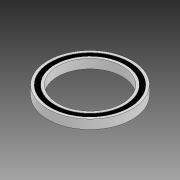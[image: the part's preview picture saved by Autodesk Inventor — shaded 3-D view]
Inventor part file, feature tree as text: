
AUTODESK INVENTOR PART (.ipt)
format: ipt  version: 2020 (Build 240168000, 168)  size: 126,464 bytes
history: native  units: mm
features: revolve x1, sketch x1
ambient origin geometry x8: Origin, YZ Plane, XZ Plane, XY Plane, X Axis, Y Axis, Z Axis, Center Point
bodies: Solid1 (feature_tree)
feature tree (2):
  revolve  "Revolution1"  [1 undecoded]
  sketch  "Sketch1"  dims[d0=25.0mm d2=7.0mm d5=32.5mm d6=0.2mm d7=2.0mm d8=90.0deg]
note: 1 required parameter value undecoded (feature->parameter linkage not recoverable at this tier; creation-order binding heuristic only, values carry confidence <= 0.55)
